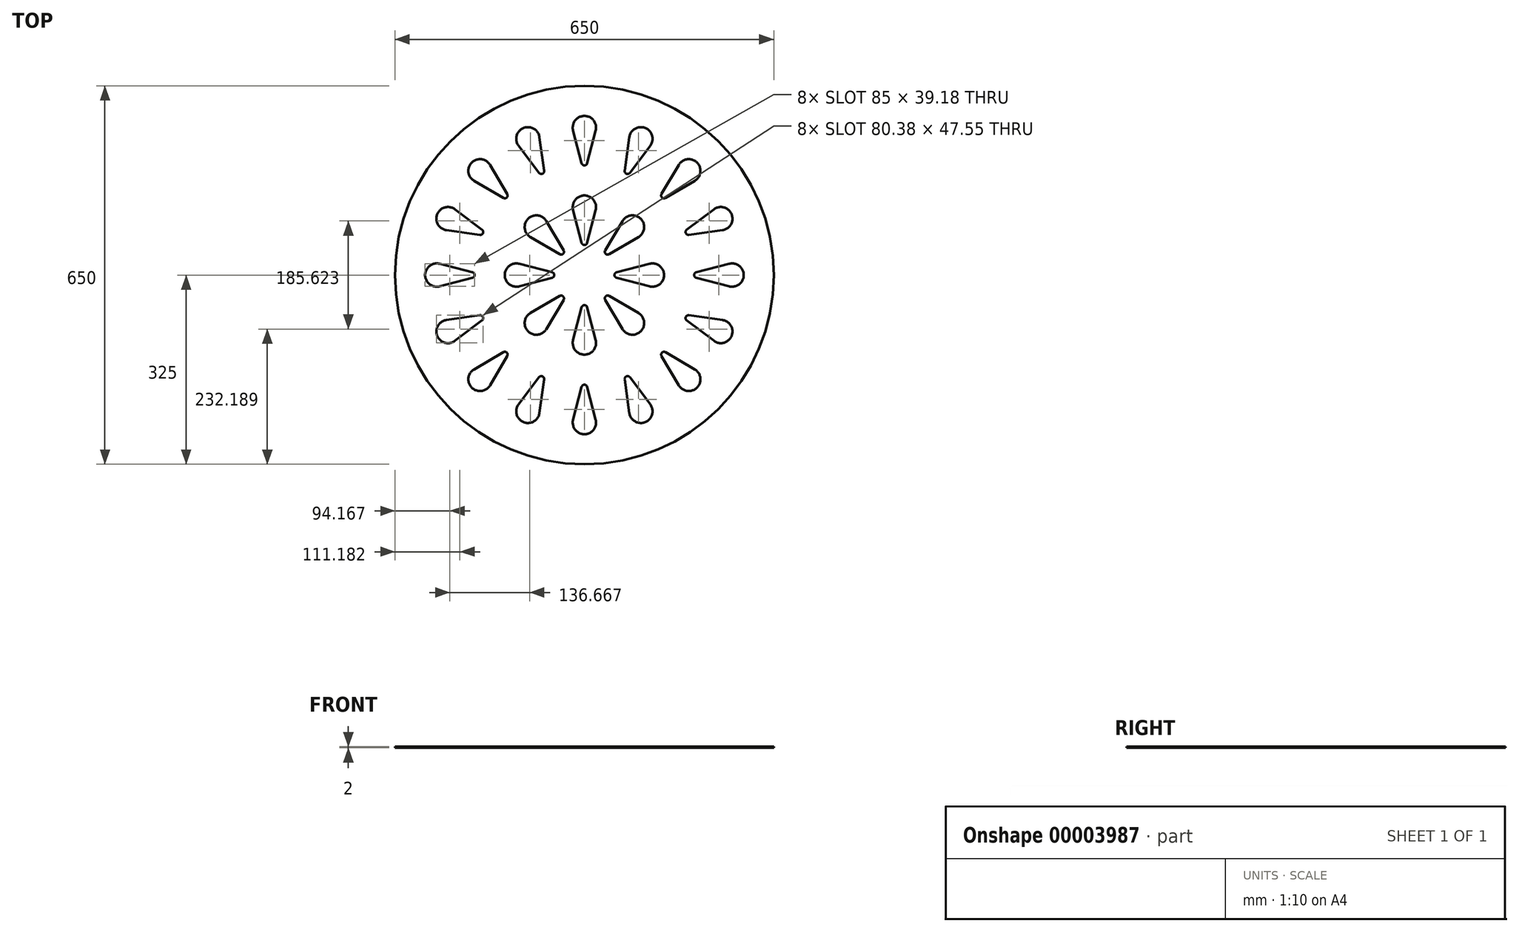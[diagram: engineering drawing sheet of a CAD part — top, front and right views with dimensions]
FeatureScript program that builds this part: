
annotation { "Feature Type Name" : "Feature", "Feature Type Description" : "" }
export const myFeature = defineFeature(function(context is Context, id is Id, definition is map)
    precondition{}
    {
        {
            var Q0;
            Q0=qCreatedBy(makeId("Top.planeOp"),FACE);
            var sketch = newSketch(context, id + "F0", { "sketchPlane" : qUnion([Q0])});
            skCircle(sketch, "E0", {"center": v(0, 0) * mm, "radius": 325 * mm});
            skLineSegment(sketch, "E1", {"start": v(4.84, 55.42) * mm, "end": v(19.36, 111.67) * mm});
            skArc(sketch, "E2", {"start": v(19.36, 111.67) * mm, "mid": v(15.81, 128.91) * mm, "end": v(0, 136.67) * mm});
            skLineSegment(sketch, "E3.0.MirrorCS", {"start": v(-4.84, 55.42) * mm, "end": v(-19.36, 111.67) * mm});
            skArc(sketch, "E4.0.MirrorCS", {"start": v(-19.36, 111.67) * mm, "mid": v(-15.81, 128.91) * mm, "end": v(0, 136.67) * mm});
            skPoint(sketch, "E5.visualSharp", {"position": v(0, 36.67) * mm});
            skArc(sketch, "E5.filletArc", {"start": v(-4.84, 55.42) * mm, "mid": v(0, 51.67) * mm, "end": v(4.84, 55.42) * mm});
            skLineSegment(sketch, "E6.0.1.0", {"start": v(4.84, 192.08) * mm, "end": v(19.36, 248.33) * mm});
            skArc(sketch, "E6.0.1.1", {"start": v(19.36, 248.33) * mm, "mid": v(15.81, 265.58) * mm, "end": v(0, 273.33) * mm});
            skArc(sketch, "E6.0.1.2", {"start": v(-19.36, 248.33) * mm, "mid": v(-15.81, 265.58) * mm, "end": v(0, 273.33) * mm});
            skLineSegment(sketch, "E6.0.1.3", {"start": v(-4.84, 192.08) * mm, "end": v(-19.36, 248.33) * mm});
            skArc(sketch, "E6.0.1.4", {"start": v(-4.84, 192.08) * mm, "mid": v(0, 188.33) * mm, "end": v(4.84, 192.08) * mm});
            skLineSegment(sketch, "E6.direction1", {"start": v(4.84, 55.42) * mm, "end": v(29.84, 55.42) * mm, "construction": true});
            skLineSegment(sketch, "E6.direction2", {"start": v(4.84, 55.42) * mm, "end": v(4.84, 192.08) * mm, "construction": true});
            skLineSegment(sketch, "E7", {"start": v(0, 273.33) * mm, "end": v(0, 325) * mm, "construction": true});
            skLineSegment(sketch, "E8", {"start": v(0, 0) * mm, "end": v(0, 51.67) * mm, "construction": true});
            skLineSegment(sketch, "E9", {"start": v(0, 136.67) * mm, "end": v(0, 188.33) * mm, "construction": true});
            skArc(sketch, "E10.1.0", {"start": v(-92.65, 65.27) * mm, "mid": v(-102.34, 79.98) * mm, "end": v(-96.64, 96.64) * mm});
            skArc(sketch, "E10.1.1", {"start": v(-65.27, 92.65) * mm, "mid": v(-79.98, 102.34) * mm, "end": v(-96.64, 96.64) * mm});
            skLineSegment(sketch, "E10.1.2", {"start": v(-35.76, 42.6) * mm, "end": v(-65.27, 92.65) * mm});
            skLineSegment(sketch, "E10.1.3", {"start": v(-42.6, 35.76) * mm, "end": v(-92.65, 65.27) * mm});
            skArc(sketch, "E10.1.4", {"start": v(-42.6, 35.76) * mm, "mid": v(-36.53, 36.53) * mm, "end": v(-35.76, 42.6) * mm});
            skArc(sketch, "E10.2.0", {"start": v(-111.67, -19.36) * mm, "mid": v(-128.91, -15.81) * mm, "end": v(-136.67, 0) * mm});
            skArc(sketch, "E10.2.1", {"start": v(-111.67, 19.36) * mm, "mid": v(-128.91, 15.81) * mm, "end": v(-136.67, 0) * mm});
            skLineSegment(sketch, "E10.2.2", {"start": v(-55.42, 4.84) * mm, "end": v(-111.67, 19.36) * mm});
            skLineSegment(sketch, "E10.2.3", {"start": v(-55.42, -4.84) * mm, "end": v(-111.67, -19.36) * mm});
            skArc(sketch, "E10.2.4", {"start": v(-55.42, -4.84) * mm, "mid": v(-51.67, 0) * mm, "end": v(-55.42, 4.84) * mm});
            skArc(sketch, "E10.3.0", {"start": v(-65.27, -92.65) * mm, "mid": v(-79.98, -102.34) * mm, "end": v(-96.64, -96.64) * mm});
            skArc(sketch, "E10.3.1", {"start": v(-92.65, -65.27) * mm, "mid": v(-102.34, -79.98) * mm, "end": v(-96.64, -96.64) * mm});
            skLineSegment(sketch, "E10.3.2", {"start": v(-42.6, -35.76) * mm, "end": v(-92.65, -65.27) * mm});
            skLineSegment(sketch, "E10.3.3", {"start": v(-35.76, -42.6) * mm, "end": v(-65.27, -92.65) * mm});
            skArc(sketch, "E10.3.4", {"start": v(-35.76, -42.6) * mm, "mid": v(-36.53, -36.53) * mm, "end": v(-42.6, -35.76) * mm});
            skArc(sketch, "E10.4.0", {"start": v(19.36, -111.67) * mm, "mid": v(15.81, -128.91) * mm, "end": v(0, -136.67) * mm});
            skArc(sketch, "E10.4.1", {"start": v(-19.36, -111.67) * mm, "mid": v(-15.81, -128.91) * mm, "end": v(0, -136.67) * mm});
            skLineSegment(sketch, "E10.4.2", {"start": v(-4.84, -55.42) * mm, "end": v(-19.36, -111.67) * mm});
            skLineSegment(sketch, "E10.4.3", {"start": v(4.84, -55.42) * mm, "end": v(19.36, -111.67) * mm});
            skArc(sketch, "E10.4.4", {"start": v(4.84, -55.42) * mm, "mid": v(0, -51.67) * mm, "end": v(-4.84, -55.42) * mm});
            skArc(sketch, "E10.5.0", {"start": v(92.65, -65.27) * mm, "mid": v(102.34, -79.98) * mm, "end": v(96.64, -96.64) * mm});
            skArc(sketch, "E10.5.1", {"start": v(65.27, -92.65) * mm, "mid": v(79.98, -102.34) * mm, "end": v(96.64, -96.64) * mm});
            skLineSegment(sketch, "E10.5.2", {"start": v(35.76, -42.6) * mm, "end": v(65.27, -92.65) * mm});
            skLineSegment(sketch, "E10.5.3", {"start": v(42.6, -35.76) * mm, "end": v(92.65, -65.27) * mm});
            skArc(sketch, "E10.5.4", {"start": v(42.6, -35.76) * mm, "mid": v(36.53, -36.53) * mm, "end": v(35.76, -42.6) * mm});
            skArc(sketch, "E10.6.0", {"start": v(111.67, 19.36) * mm, "mid": v(128.91, 15.81) * mm, "end": v(136.67, 0) * mm});
            skArc(sketch, "E10.6.1", {"start": v(111.67, -19.36) * mm, "mid": v(128.91, -15.81) * mm, "end": v(136.67, 0) * mm});
            skLineSegment(sketch, "E10.6.2", {"start": v(55.42, -4.84) * mm, "end": v(111.67, -19.36) * mm});
            skLineSegment(sketch, "E10.6.3", {"start": v(55.42, 4.84) * mm, "end": v(111.67, 19.36) * mm});
            skArc(sketch, "E10.6.4", {"start": v(55.42, 4.84) * mm, "mid": v(51.67, 0) * mm, "end": v(55.42, -4.84) * mm});
            skArc(sketch, "E10.7.0", {"start": v(65.27, 92.65) * mm, "mid": v(79.98, 102.34) * mm, "end": v(96.64, 96.64) * mm});
            skArc(sketch, "E10.7.1", {"start": v(92.65, 65.27) * mm, "mid": v(102.34, 79.98) * mm, "end": v(96.64, 96.64) * mm});
            skLineSegment(sketch, "E10.7.2", {"start": v(42.6, 35.76) * mm, "end": v(92.65, 65.27) * mm});
            skLineSegment(sketch, "E10.7.3", {"start": v(35.76, 42.6) * mm, "end": v(65.27, 92.65) * mm});
            skArc(sketch, "E10.7.4", {"start": v(35.76, 42.6) * mm, "mid": v(36.53, 36.53) * mm, "end": v(42.6, 35.76) * mm});
            skArc(sketch, "E11.1.0", {"start": v(-77.14, 236.84) * mm, "mid": v(-87.03, 251.42) * mm, "end": v(-104.6, 252.53) * mm});
            skArc(sketch, "E11.1.1", {"start": v(-112.92, 222.02) * mm, "mid": v(-116.24, 239.31) * mm, "end": v(-104.6, 252.53) * mm});
            skLineSegment(sketch, "E11.1.2", {"start": v(-77.98, 175.6) * mm, "end": v(-112.92, 222.02) * mm});
            skLineSegment(sketch, "E11.1.3", {"start": v(-69.03, 179.31) * mm, "end": v(-77.14, 236.84) * mm});
            skArc(sketch, "E11.1.4", {"start": v(-77.98, 175.6) * mm, "mid": v(-72.07, 174) * mm, "end": v(-69.03, 179.31) * mm});
            skArc(sketch, "E11.2.0", {"start": v(-161.9, 189.3) * mm, "mid": v(-176.61, 198.97) * mm, "end": v(-193.28, 193.28) * mm});
            skArc(sketch, "E11.2.1", {"start": v(-189.3, 161.9) * mm, "mid": v(-198.97, 176.61) * mm, "end": v(-193.28, 193.28) * mm});
            skLineSegment(sketch, "E11.2.2", {"start": v(-139.25, 132.4) * mm, "end": v(-189.3, 161.9) * mm});
            skLineSegment(sketch, "E11.2.3", {"start": v(-132.4, 139.25) * mm, "end": v(-161.9, 189.3) * mm});
            skArc(sketch, "E11.2.4", {"start": v(-139.25, 132.4) * mm, "mid": v(-133.17, 133.17) * mm, "end": v(-132.4, 139.25) * mm});
            skArc(sketch, "E11.3.0", {"start": v(-222.02, 112.92) * mm, "mid": v(-239.31, 116.24) * mm, "end": v(-252.53, 104.6) * mm});
            skArc(sketch, "E11.3.1", {"start": v(-236.84, 77.14) * mm, "mid": v(-251.42, 87.03) * mm, "end": v(-252.53, 104.6) * mm});
            skLineSegment(sketch, "E11.3.2", {"start": v(-179.31, 69.03) * mm, "end": v(-236.84, 77.14) * mm});
            skLineSegment(sketch, "E11.3.3", {"start": v(-175.6, 77.98) * mm, "end": v(-222.02, 112.92) * mm});
            skArc(sketch, "E11.3.4", {"start": v(-179.31, 69.03) * mm, "mid": v(-174, 72.07) * mm, "end": v(-175.6, 77.98) * mm});
            skArc(sketch, "E11.4.0", {"start": v(-248.33, 19.36) * mm, "mid": v(-265.58, 15.81) * mm, "end": v(-273.33, 0) * mm});
            skArc(sketch, "E11.4.1", {"start": v(-248.33, -19.36) * mm, "mid": v(-265.58, -15.81) * mm, "end": v(-273.33, 0) * mm});
            skLineSegment(sketch, "E11.4.2", {"start": v(-192.08, -4.84) * mm, "end": v(-248.33, -19.36) * mm});
            skLineSegment(sketch, "E11.4.3", {"start": v(-192.08, 4.84) * mm, "end": v(-248.33, 19.36) * mm});
            skArc(sketch, "E11.4.4", {"start": v(-192.08, -4.84) * mm, "mid": v(-188.33, 0) * mm, "end": v(-192.08, 4.84) * mm});
            skArc(sketch, "E11.5.0", {"start": v(-236.84, -77.14) * mm, "mid": v(-251.42, -87.03) * mm, "end": v(-252.53, -104.6) * mm});
            skArc(sketch, "E11.5.1", {"start": v(-222.02, -112.92) * mm, "mid": v(-239.31, -116.24) * mm, "end": v(-252.53, -104.6) * mm});
            skLineSegment(sketch, "E11.5.2", {"start": v(-175.6, -77.98) * mm, "end": v(-222.02, -112.92) * mm});
            skLineSegment(sketch, "E11.5.3", {"start": v(-179.31, -69.03) * mm, "end": v(-236.84, -77.14) * mm});
            skArc(sketch, "E11.5.4", {"start": v(-175.6, -77.98) * mm, "mid": v(-174, -72.07) * mm, "end": v(-179.31, -69.03) * mm});
            skArc(sketch, "E11.6.0", {"start": v(-189.3, -161.9) * mm, "mid": v(-198.97, -176.61) * mm, "end": v(-193.28, -193.28) * mm});
            skArc(sketch, "E11.6.1", {"start": v(-161.9, -189.3) * mm, "mid": v(-176.61, -198.97) * mm, "end": v(-193.28, -193.28) * mm});
            skLineSegment(sketch, "E11.6.2", {"start": v(-132.4, -139.25) * mm, "end": v(-161.9, -189.3) * mm});
            skLineSegment(sketch, "E11.6.3", {"start": v(-139.25, -132.4) * mm, "end": v(-189.3, -161.9) * mm});
            skArc(sketch, "E11.6.4", {"start": v(-132.4, -139.25) * mm, "mid": v(-133.17, -133.17) * mm, "end": v(-139.25, -132.4) * mm});
            skArc(sketch, "E11.7.0", {"start": v(-112.92, -222.02) * mm, "mid": v(-116.24, -239.31) * mm, "end": v(-104.6, -252.53) * mm});
            skArc(sketch, "E11.7.1", {"start": v(-77.14, -236.84) * mm, "mid": v(-87.03, -251.42) * mm, "end": v(-104.6, -252.53) * mm});
            skLineSegment(sketch, "E11.7.2", {"start": v(-69.03, -179.31) * mm, "end": v(-77.14, -236.84) * mm});
            skLineSegment(sketch, "E11.7.3", {"start": v(-77.98, -175.6) * mm, "end": v(-112.92, -222.02) * mm});
            skArc(sketch, "E11.7.4", {"start": v(-69.03, -179.31) * mm, "mid": v(-72.07, -174) * mm, "end": v(-77.98, -175.6) * mm});
            skArc(sketch, "E11.8.0", {"start": v(-19.36, -248.33) * mm, "mid": v(-15.81, -265.58) * mm, "end": v(0, -273.33) * mm});
            skArc(sketch, "E11.8.1", {"start": v(19.36, -248.33) * mm, "mid": v(15.81, -265.58) * mm, "end": v(0, -273.33) * mm});
            skLineSegment(sketch, "E11.8.2", {"start": v(4.84, -192.08) * mm, "end": v(19.36, -248.33) * mm});
            skLineSegment(sketch, "E11.8.3", {"start": v(-4.84, -192.08) * mm, "end": v(-19.36, -248.33) * mm});
            skArc(sketch, "E11.8.4", {"start": v(4.84, -192.08) * mm, "mid": v(0, -188.33) * mm, "end": v(-4.84, -192.08) * mm});
            skArc(sketch, "E11.9.0", {"start": v(77.14, -236.84) * mm, "mid": v(87.03, -251.42) * mm, "end": v(104.6, -252.53) * mm});
            skArc(sketch, "E11.9.1", {"start": v(112.92, -222.02) * mm, "mid": v(116.24, -239.31) * mm, "end": v(104.6, -252.53) * mm});
            skLineSegment(sketch, "E11.9.2", {"start": v(77.98, -175.6) * mm, "end": v(112.92, -222.02) * mm});
            skLineSegment(sketch, "E11.9.3", {"start": v(69.03, -179.31) * mm, "end": v(77.14, -236.84) * mm});
            skArc(sketch, "E11.9.4", {"start": v(77.98, -175.6) * mm, "mid": v(72.07, -174) * mm, "end": v(69.03, -179.31) * mm});
            skArc(sketch, "E11.10.0", {"start": v(161.9, -189.3) * mm, "mid": v(176.61, -198.97) * mm, "end": v(193.28, -193.28) * mm});
            skArc(sketch, "E11.10.1", {"start": v(189.3, -161.9) * mm, "mid": v(198.97, -176.61) * mm, "end": v(193.28, -193.28) * mm});
            skLineSegment(sketch, "E11.10.2", {"start": v(139.25, -132.4) * mm, "end": v(189.3, -161.9) * mm});
            skLineSegment(sketch, "E11.10.3", {"start": v(132.4, -139.25) * mm, "end": v(161.9, -189.3) * mm});
            skArc(sketch, "E11.10.4", {"start": v(139.25, -132.4) * mm, "mid": v(133.17, -133.17) * mm, "end": v(132.4, -139.25) * mm});
            skArc(sketch, "E11.11.0", {"start": v(222.02, -112.92) * mm, "mid": v(239.31, -116.24) * mm, "end": v(252.53, -104.6) * mm});
            skArc(sketch, "E11.11.1", {"start": v(236.84, -77.14) * mm, "mid": v(251.42, -87.03) * mm, "end": v(252.53, -104.6) * mm});
            skLineSegment(sketch, "E11.11.2", {"start": v(179.31, -69.03) * mm, "end": v(236.84, -77.14) * mm});
            skLineSegment(sketch, "E11.11.3", {"start": v(175.6, -77.98) * mm, "end": v(222.02, -112.92) * mm});
            skArc(sketch, "E11.11.4", {"start": v(179.31, -69.03) * mm, "mid": v(174, -72.07) * mm, "end": v(175.6, -77.98) * mm});
            skArc(sketch, "E11.12.0", {"start": v(248.33, -19.36) * mm, "mid": v(265.58, -15.81) * mm, "end": v(273.33, 0) * mm});
            skArc(sketch, "E11.12.1", {"start": v(248.33, 19.36) * mm, "mid": v(265.58, 15.81) * mm, "end": v(273.33, 0) * mm});
            skLineSegment(sketch, "E11.12.2", {"start": v(192.08, 4.84) * mm, "end": v(248.33, 19.36) * mm});
            skLineSegment(sketch, "E11.12.3", {"start": v(192.08, -4.84) * mm, "end": v(248.33, -19.36) * mm});
            skArc(sketch, "E11.12.4", {"start": v(192.08, 4.84) * mm, "mid": v(188.33, 0) * mm, "end": v(192.08, -4.84) * mm});
            skArc(sketch, "E11.13.0", {"start": v(236.84, 77.14) * mm, "mid": v(251.42, 87.03) * mm, "end": v(252.53, 104.6) * mm});
            skArc(sketch, "E11.13.1", {"start": v(222.02, 112.92) * mm, "mid": v(239.31, 116.24) * mm, "end": v(252.53, 104.6) * mm});
            skLineSegment(sketch, "E11.13.2", {"start": v(175.6, 77.98) * mm, "end": v(222.02, 112.92) * mm});
            skLineSegment(sketch, "E11.13.3", {"start": v(179.31, 69.03) * mm, "end": v(236.84, 77.14) * mm});
            skArc(sketch, "E11.13.4", {"start": v(175.6, 77.98) * mm, "mid": v(174, 72.07) * mm, "end": v(179.31, 69.03) * mm});
            skArc(sketch, "E11.14.0", {"start": v(189.3, 161.9) * mm, "mid": v(198.97, 176.61) * mm, "end": v(193.28, 193.28) * mm});
            skArc(sketch, "E11.14.1", {"start": v(161.9, 189.3) * mm, "mid": v(176.61, 198.97) * mm, "end": v(193.28, 193.28) * mm});
            skLineSegment(sketch, "E11.14.2", {"start": v(132.4, 139.25) * mm, "end": v(161.9, 189.3) * mm});
            skLineSegment(sketch, "E11.14.3", {"start": v(139.25, 132.4) * mm, "end": v(189.3, 161.9) * mm});
            skArc(sketch, "E11.14.4", {"start": v(132.4, 139.25) * mm, "mid": v(133.17, 133.17) * mm, "end": v(139.25, 132.4) * mm});
            skArc(sketch, "E11.15.0", {"start": v(112.92, 222.02) * mm, "mid": v(116.24, 239.31) * mm, "end": v(104.6, 252.53) * mm});
            skArc(sketch, "E11.15.1", {"start": v(77.14, 236.84) * mm, "mid": v(87.03, 251.42) * mm, "end": v(104.6, 252.53) * mm});
            skLineSegment(sketch, "E11.15.2", {"start": v(69.03, 179.31) * mm, "end": v(77.14, 236.84) * mm});
            skLineSegment(sketch, "E11.15.3", {"start": v(77.98, 175.6) * mm, "end": v(112.92, 222.02) * mm});
            skArc(sketch, "E11.15.4", {"start": v(69.03, 179.31) * mm, "mid": v(72.07, 174) * mm, "end": v(77.98, 175.6) * mm});
            skSolve(sketch);
        }
        {
            var Q0;
            Q0=makeQuery(id+"F0.imprint","IMPRINT",FACE,{"disambiguationData":[TD([[makeQuery(id+"F0.imprint","IMPRINT",EDGE,{"derivedFrom":sQuery(id+"F0.wireOp",EDGE,"E0")}),1.0]])]});
            extrude(context, id + "F1", {"entities" : qUnion([Q0]), "depth" : 2 * mm});
        }
    });
